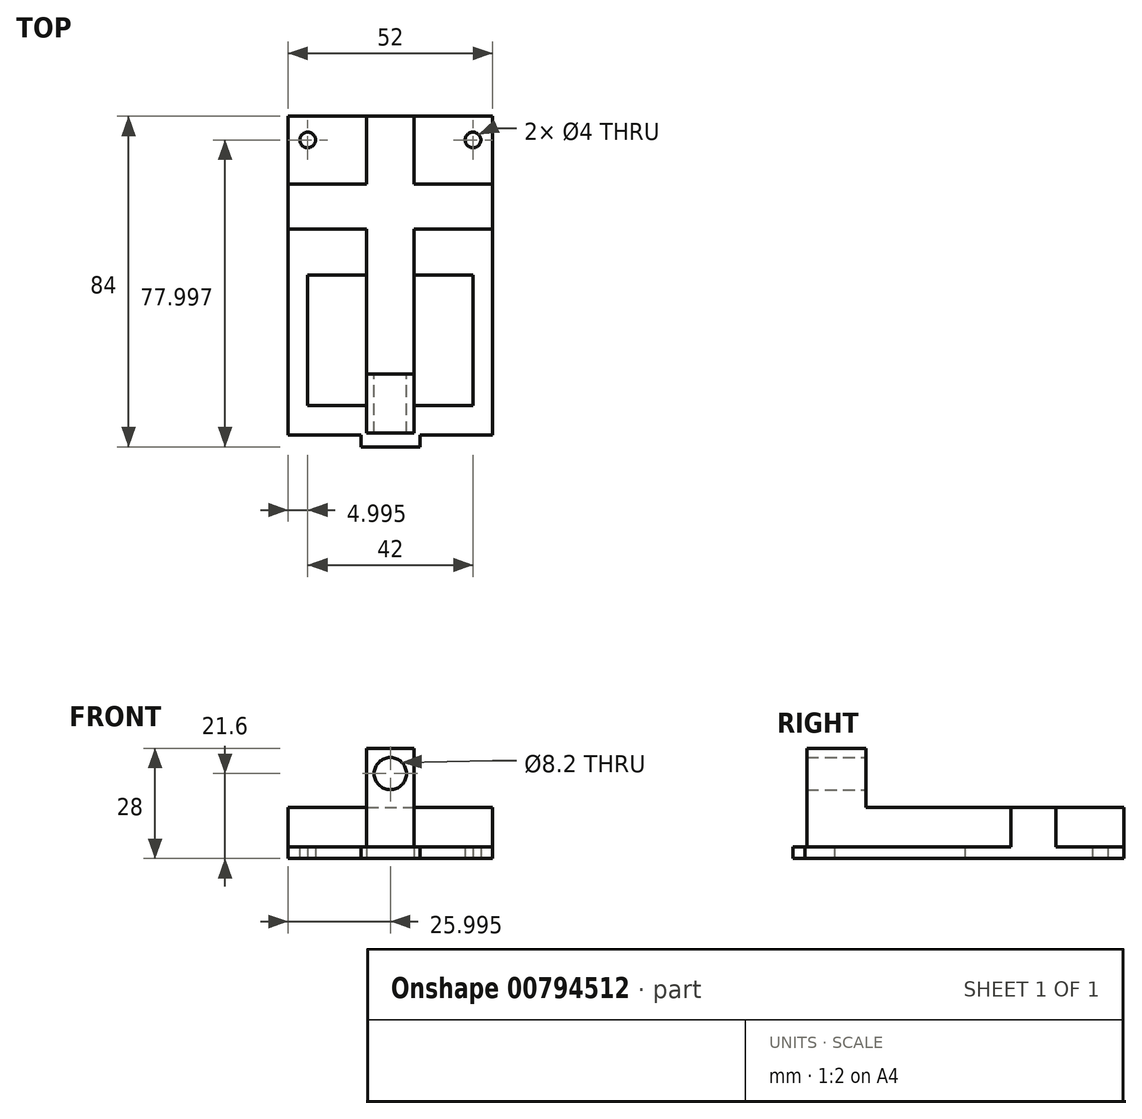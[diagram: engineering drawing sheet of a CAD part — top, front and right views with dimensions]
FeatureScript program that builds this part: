
annotation { "Feature Type Name" : "Feature", "Feature Type Description" : "" }
export const myFeature = defineFeature(function(context is Context, id is Id, definition is map)
    precondition{}
    {
        {
            var Q0;
            Q0=qCreatedBy(makeId("Top.planeOp"),FACE);
            var sketch = newSketch(context, id + "F0", { "sketchPlane" : qUnion([Q0])});
            skLineSegment(sketch, "E0.bottom", {"start": v(-17.6, -40.7) * mm, "end": v(-69.6, -40.7) * mm});
            skLineSegment(sketch, "E0.top", {"start": v(-17.6, 40.3) * mm, "end": v(-69.6, 40.3) * mm});
            skLineSegment(sketch, "E0.left", {"start": v(-17.6, -40.7) * mm, "end": v(-17.6, 40.3) * mm});
            skLineSegment(sketch, "E0.right", {"start": v(-69.6, -40.7) * mm, "end": v(-69.6, 40.3) * mm});
            skPoint(sketch, "E0.middle", {"position": v(-43.6, -0.2) * mm});
            skLineSegment(sketch, "E1.0", {"start": v(-17.6, 34.3) * mm, "end": v(-69.6, 34.3) * mm, "construction": true});
            skLineSegment(sketch, "E2.0", {"start": v(-64.6, -40.7) * mm, "end": v(-64.6, 0) * mm, "construction": true});
            skLineSegment(sketch, "E3.0", {"start": v(-22.6, -40.7) * mm, "end": v(-22.6, 0) * mm, "construction": true});
            skCircle(sketch, "E4", {"center": v(-64.6, 34.3) * mm, "radius": 2 * mm});
            skCircle(sketch, "E5", {"center": v(-22.6, 34.3) * mm, "radius": 2 * mm});
            skLineSegment(sketch, "E6", {"start": v(-43.6, -40.7) * mm, "end": v(-43.6, -43.7) * mm, "construction": true});
            skLineSegment(sketch, "E7", {"start": v(-51.1, -43.7) * mm, "end": v(-43.6, -43.7) * mm});
            skLineSegment(sketch, "E8", {"start": v(-43.6, -43.7) * mm, "end": v(-36.1, -43.7) * mm});
            skLineSegment(sketch, "E9", {"start": v(-51.1, -43.7) * mm, "end": v(-51.1, -40.7) * mm});
            skLineSegment(sketch, "E10", {"start": v(-36.1, -43.7) * mm, "end": v(-36.1, -40.7) * mm});
            skLineSegment(sketch, "E11.bottom", {"start": v(-64.6, -33.21) * mm, "end": v(-49.6, -33.21) * mm});
            skLineSegment(sketch, "E11.left", {"start": v(-64.6, -33.21) * mm, "end": v(-64.6, 0) * mm});
            skLineSegment(sketch, "E11.right", {"start": v(-22.6, -33.21) * mm, "end": v(-22.6, 0) * mm});
            skLineSegment(sketch, "E12", {"start": v(-64.6, 0) * mm, "end": v(-49.6, 0) * mm});
            skPoint(sketch, "E12.startSnap0", {"position": v(-64.6, -1.81) * mm});
            skLineSegment(sketch, "E13.trimOffspring", {"start": v(-64.6, 29.58) * mm, "end": v(-64.6, 40.3) * mm, "construction": true});
            skLineSegment(sketch, "E14.trimOffspring", {"start": v(-22.6, 29.58) * mm, "end": v(-22.6, 40.3) * mm, "construction": true});
            skLineSegment(sketch, "E15", {"start": v(-43.6, -0.2) * mm, "end": v(-43.6, -40.7) * mm, "construction": true});
            skLineSegment(sketch, "E16.0", {"start": v(-49.6, 0) * mm, "end": v(-49.6, -33.21) * mm});
            skLineSegment(sketch, "E17.0", {"start": v(-37.6, 0) * mm, "end": v(-37.6, -33.21) * mm});
            skLineSegment(sketch, "E18.trimOffspring", {"start": v(-37.6, 0) * mm, "end": v(-22.6, 0) * mm});
            skLineSegment(sketch, "E19.trimOffspring", {"start": v(-37.6, -33.21) * mm, "end": v(-22.6, -33.21) * mm});
            skSolve(sketch);
        }
        {
            var Q0;
            Q0=makeQuery(id+"F0.imprint","IMPRINT",FACE,{"disambiguationData":[TD([[makeQuery(id+"F0.imprint","IMPRINT",EDGE,{"derivedFrom":sQuery(id+"F0.wireOp",EDGE,"E0.top")}),1.0]])]});
            var Q1;
            Q1=makeQuery(id+"F0.imprint","IMPRINT",FACE,{"disambiguationData":[TD([[makeQuery(id+"F0.imprint","IMPRINT",EDGE,{"derivedFrom":sQuery(id+"F0.wireOp",EDGE,"E7")}),1.0]])]});
            extrude(context, id + "F1", {"entities" : qUnion([Q0, Q1]), "depth" : 3 * mm, "offsetDistance" : 25 * mm});
        }
        {
            var Q0;
            Q0=makeQuery(id+"F1.opExtrude","CAP_FACE",FACE,{"disambiguationData":[OSD([sQuery(id+"F0.wireOp",EDGE,"E0.bottom"),sQuery(id+"F0.wireOp",EDGE,"E0.top"),sQuery(id+"F0.wireOp",EDGE,"E0.left"),sQuery(id+"F0.wireOp",EDGE,"E0.right"),sQuery(id+"F0.wireOp",EDGE,"E4"),sQuery(id+"F0.wireOp",EDGE,"E5"),sQuery(id+"F0.wireOp",EDGE,"E7"),sQuery(id+"F0.wireOp",EDGE,"E8"),sQuery(id+"F0.wireOp",EDGE,"E9"),sQuery(id+"F0.wireOp",EDGE,"E10"),sQuery(id+"F0.wireOp",EDGE,"E11.bottom"),sQuery(id+"F0.wireOp",EDGE,"E11.left"),sQuery(id+"F0.wireOp",EDGE,"E11.right"),sQuery(id+"F0.wireOp",EDGE,"E12"),sQuery(id+"F0.wireOp",EDGE,"E16.0"),sQuery(id+"F0.wireOp",EDGE,"E17.0"),sQuery(id+"F0.wireOp",EDGE,"E18.trimOffspring"),sQuery(id+"F0.wireOp",EDGE,"E19.trimOffspring")])],"isStart":false});
            var sketch = newSketch(context, id + "F2", { "sketchPlane" : qUnion([Q0])});
            skLineSegment(sketch, "E20.0", {"start": v(-49.6, 0) * mm, "end": v(-49.6, -33.21) * mm});
            skLineSegment(sketch, "E21", {"start": v(-49.6, -33.21) * mm, "end": v(-49.6, -40.21) * mm});
            skLineSegment(sketch, "E22", {"start": v(-37.6, -33.21) * mm, "end": v(-37.6, -40.21) * mm});
            skLineSegment(sketch, "E23", {"start": v(-49.6, -40.21) * mm, "end": v(-37.6, -40.21) * mm});
            skLineSegment(sketch, "E24", {"start": v(-49.6, 0) * mm, "end": v(-49.6, 11.61) * mm});
            skLineSegment(sketch, "E25", {"start": v(-37.6, 0) * mm, "end": v(-37.6, 11.61) * mm});
            skLineSegment(sketch, "E26", {"start": v(-17.6, 11.61) * mm, "end": v(-37.6, 11.61) * mm});
            skLineSegment(sketch, "E27", {"start": v(-17.6, 23.02) * mm, "end": v(-37.6, 23.02) * mm});
            skLineSegment(sketch, "E28.trimOffspring", {"start": v(-49.6, 23.02) * mm, "end": v(-49.6, 40.3) * mm});
            skLineSegment(sketch, "E29.trimOffspring", {"start": v(-49.6, 23.02) * mm, "end": v(-69.6, 23.02) * mm});
            skLineSegment(sketch, "E30.trimOffspring", {"start": v(-37.6, 23.02) * mm, "end": v(-37.6, 40.3) * mm});
            skLineSegment(sketch, "E31.trimOffspring", {"start": v(-49.6, 11.61) * mm, "end": v(-69.6, 11.61) * mm});
            skSolve(sketch);
        }
        {
            var Q0;
            Q0=makeQuery(id+"F2.imprint","IMPRINT",FACE,{"disambiguationData":[TD([[makeQuery(id+"F2.imprint","IMPRINT",EDGE,{"derivedFrom":sQuery(id+"F2.wireOp",EDGE,"E20.0")}),1.0]])]});
            extrude(context, id + "F3", {"entities" : qUnion([Q0]), "operationType" : NewBodyOperationType.ADD, "depth" : 10 * mm, "offsetDistance" : 25 * mm});
        }
        {
            var Q0;
            Q0=makeQuery(id+"F3.opExtrude","CAP_FACE",FACE,{"disambiguationData":[OSD([sQuery(id+"F0.wireOp",EDGE,"E0.top"),sQuery(id+"F0.wireOp",EDGE,"E0.left"),sQuery(id+"F0.wireOp",EDGE,"E0.right"),sQuery(id+"F0.wireOp",EDGE,"E17.0"),sQuery(id+"F2.wireOp",EDGE,"E20.0"),sQuery(id+"F2.wireOp",EDGE,"E21"),sQuery(id+"F2.wireOp",EDGE,"E22"),sQuery(id+"F2.wireOp",EDGE,"E23"),sQuery(id+"F2.wireOp",EDGE,"E24"),sQuery(id+"F2.wireOp",EDGE,"E25"),sQuery(id+"F2.wireOp",EDGE,"E26"),sQuery(id+"F2.wireOp",EDGE,"E27"),sQuery(id+"F2.wireOp",EDGE,"E28.trimOffspring"),sQuery(id+"F2.wireOp",EDGE,"E29.trimOffspring"),sQuery(id+"F2.wireOp",EDGE,"E30.trimOffspring"),sQuery(id+"F2.wireOp",EDGE,"E31.trimOffspring")])],"isStart":false});
            var sketch = newSketch(context, id + "F4", { "sketchPlane" : qUnion([Q0])});
            skLineSegment(sketch, "E32", {"start": v(-49.6, -25.21) * mm, "end": v(-37.6, -25.21) * mm});
            skLineSegment(sketch, "E33", {"start": v(-46.42, -25.21) * mm, "end": v(-46.42, -40.21) * mm, "construction": true});
            skSolve(sketch);
        }
        {
            var Q0;
            {var subQ0=sQuery(id+"F4.wireOp",EDGE,"E32");Q0=makeQuery(id+"F4.imprint","IMPRINT",FACE,{"disambiguationData":[TD([[makeQuery(id+"F4.imprint","IMPRINT",EDGE,{"derivedFrom":subQ0}),-1.0]])]});}
            extrude(context, id + "F5", {"entities" : qUnion([Q0]), "operationType" : NewBodyOperationType.ADD, "depth" : 15 * mm, "offsetDistance" : 25 * mm});
        }
        {
            var Q0;
            Q0=makeQuery(id+"F5.opExtrude","SWEPT_FACE",FACE,{"disambiguationData":[OSD([sQuery(id+"F4.wireOp",EDGE,"E32")])]});
            var sketch = newSketch(context, id + "F6", { "sketchPlane" : qUnion([Q0])});
            skLineSegment(sketch, "E34", {"start": v(49.6, 28) * mm, "end": v(49.6, 27.6) * mm, "construction": true});
            skLineSegment(sketch, "E35", {"start": v(49.6, 27.6) * mm, "end": v(37.6, 27.6) * mm, "construction": true});
            skLineSegment(sketch, "E36", {"start": v(49.6, 27.6) * mm, "end": v(37.6, 15.6) * mm, "construction": true});
            skCircle(sketch, "E37", {"center": v(43.6, 21.6) * mm, "radius": 4.1 * mm});
            skLineSegment(sketch, "E38", {"start": v(43.6, 13) * mm, "end": v(43.6, 17.5) * mm, "construction": true});
            skSolve(sketch);
        }
        {
            var Q0;
            Q0=makeQuery(id+"F6.imprint","IMPRINT",FACE,{"disambiguationData":[TD([[makeQuery(id+"F6.imprint","IMPRINT",EDGE,{"derivedFrom":sQuery(id+"F6.wireOp",EDGE,"E37")}),1.0]])]});
            extrude(context, id + "F7", {"entities" : qUnion([Q0]), "operationType" : NewBodyOperationType.REMOVE, "oppositeDirection" : true, "depth" : 25 * mm, "offsetDistance" : 25 * mm});
        }
    });
